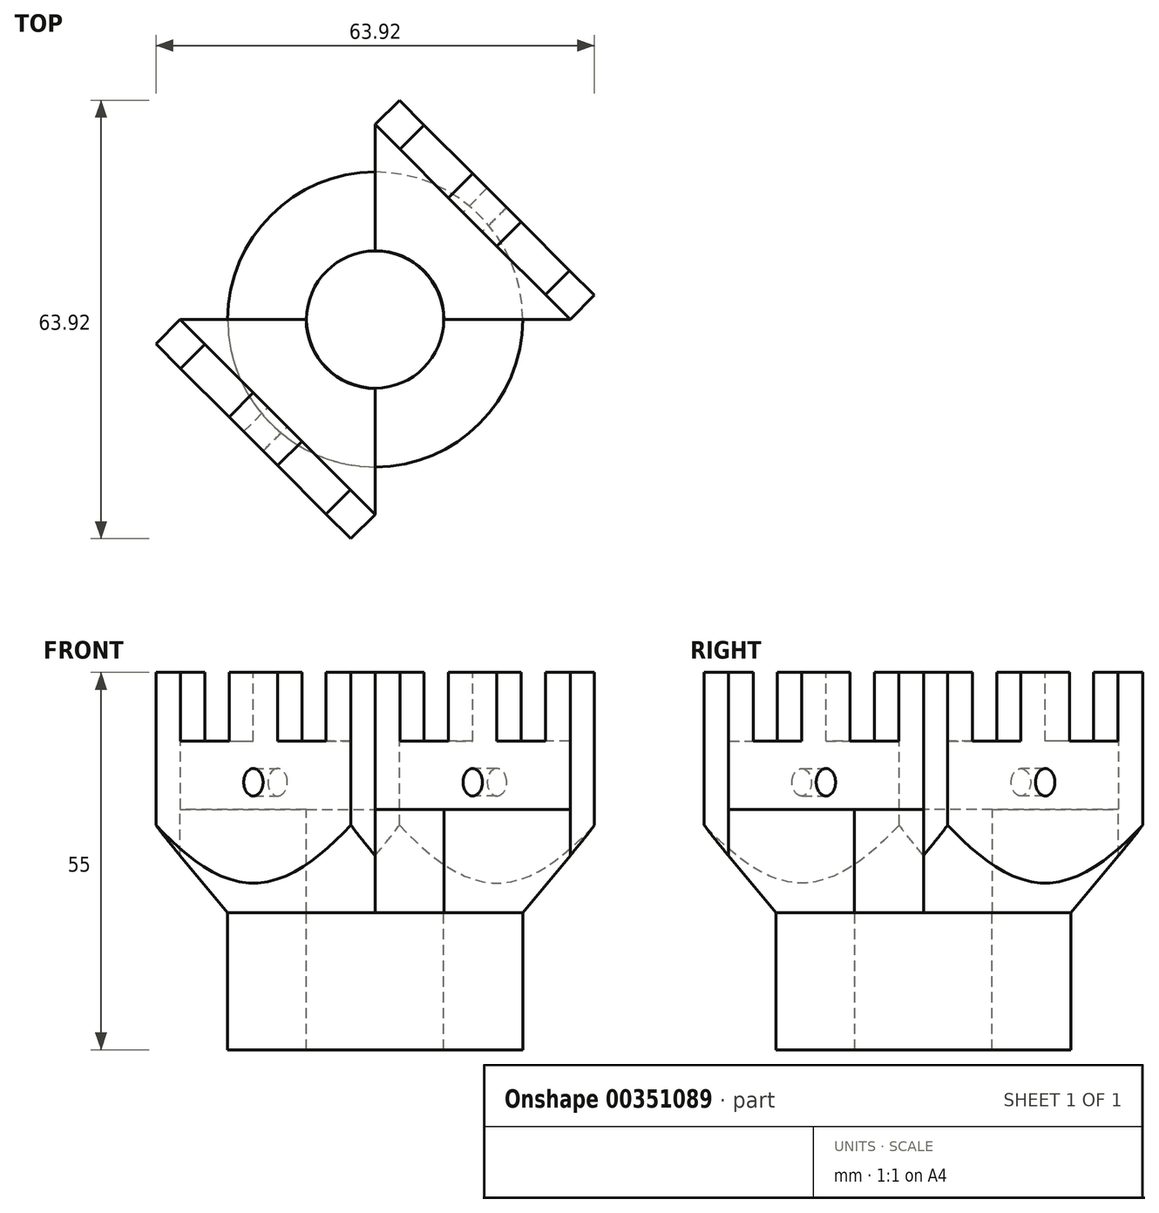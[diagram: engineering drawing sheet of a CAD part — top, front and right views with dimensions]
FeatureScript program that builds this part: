
annotation { "Feature Type Name" : "Feature", "Feature Type Description" : "" }
export const myFeature = defineFeature(function(context is Context, id is Id, definition is map)
    precondition{}
    {
        {
            var Q0;
            Q0=qCreatedBy(makeId("Top.planeOp"),FACE);
            var sketch = newSketch(context, id + "F0", { "sketchPlane" : qUnion([Q0])});
            skCircle(sketch, "E0", {"center": v(0, 0) * mm, "radius": 21.5 * mm});
            skSolve(sketch);
        }
        {
            var Q0;
            Q0=makeQuery(id+"F0.imprint","IMPRINT",FACE,{"disambiguationData":[TD([[makeQuery(id+"F0.imprint","IMPRINT",EDGE,{"derivedFrom":sQuery(id+"F0.wireOp",EDGE,"E0")}),1.0]])]});
            extrude(context, id + "F1", {"entities" : qUnion([Q0]), "depth" : -20 * mm});
        }
        {
            var Q0;
            Q0=makeQuery(id+"F1.opExtrude","CAP_FACE",FACE,{"disambiguationData":[OSD([sQuery(id+"F0.wireOp",EDGE,"E0")])],"isStart":true});
            var sketch = newSketch(context, id + "F2", { "sketchPlane" : qUnion([Q0])});
            skCircle(sketch, "E1", {"center": v(0, 0) * mm, "radius": 10 * mm});
            skSolve(sketch);
        }
        {
            var Q0;
            Q0=makeQuery(id+"F2.imprint","IMPRINT",FACE,{"disambiguationData":[TD([[makeQuery(id+"F2.imprint","IMPRINT",EDGE,{"derivedFrom":sQuery(id+"F2.wireOp",EDGE,"E1")}),1.0]])]});
            extrude(context, id + "F3", {"entities" : qUnion([Q0]), "operationType" : NewBodyOperationType.REMOVE, "endBound" : BoundingType.THROUGH_ALL, "oppositeDirection" : true, "depth" : 25 * mm});
        }
        {
            var Q0;
            Q0=makeQuery(id+"F1.opExtrude","CAP_FACE",FACE,{"disambiguationData":[OSD([sQuery(id+"F0.wireOp",EDGE,"E0")])],"isStart":true});
            var sketch = newSketch(context, id + "F4", { "sketchPlane" : qUnion([Q0])});
            skLineSegment(sketch, "E2.bottom", {"start": v(20.1, 20.1) * mm, "end": v(-20.1, 20.1) * mm, "construction": true});
            skLineSegment(sketch, "E2.top", {"start": v(20.1, -20.1) * mm, "end": v(-20.1, -20.1) * mm, "construction": true});
            skLineSegment(sketch, "E2.left", {"start": v(20.1, 20.1) * mm, "end": v(20.1, -20.1) * mm, "construction": true});
            skLineSegment(sketch, "E2.right", {"start": v(-20.1, 20.1) * mm, "end": v(-20.1, -20.1) * mm, "construction": true});
            skPoint(sketch, "E2.middle", {"position": v(0, 0) * mm});
            skLineSegment(sketch, "E3", {"start": v(0, 0) * mm, "end": v(20.1, 0) * mm, "construction": true});
            skLineSegment(sketch, "E4", {"start": v(20.1, 0) * mm, "end": v(21.5, 0) * mm, "construction": true});
            skSolve(sketch);
        }
        {
            var Q0;
            Q0=qCreatedBy(makeId("Front.planeOp"),FACE);
            var sketch = newSketch(context, id + "F5", { "sketchPlane" : qUnion([Q0])});
            skLineSegment(sketch, "E5", {"start": v(10.05, 0) * mm, "end": v(10.05, 15) * mm});
            skLineSegment(sketch, "E6", {"start": v(10.05, 15) * mm, "end": v(26.57, 15) * mm});
            skLineSegment(sketch, "E7", {"start": v(31.85, 12.37) * mm, "end": v(21.5, 0) * mm});
            skLineSegment(sketch, "E8", {"start": v(21.5, 0) * mm, "end": v(10.05, 0) * mm});
            skPoint(sketch, "E9.visualSharp", {"position": v(34.05, 15) * mm});
            skLineSegment(sketch, "E10", {"start": v(0, 0) * mm, "end": v(0, 17.69) * mm, "construction": true});
            skLineSegment(sketch, "E11", {"start": v(31.85, 12.37) * mm, "end": v(34.05, 15) * mm});
            skLineSegment(sketch, "E12", {"start": v(26.57, 15) * mm, "end": v(34.05, 15) * mm});
            skSolve(sketch);
        }
        {
            var Q0;
            Q0=makeQuery(id+"F5.imprint","IMPRINT",FACE,{"disambiguationData":[TD([[makeQuery(id+"F5.imprint","IMPRINT",EDGE,{"derivedFrom":sQuery(id+"F5.wireOp",EDGE,"E5")}),-1.0]])]});
            var Q1;
            Q1=sQuery(id+"F5.wireOp",EDGE,"E10");
            revolve(context, id + "F6", {"operationType" : NewBodyOperationType.ADD, "entities" : qUnion([Q0]), "axis" : qUnion([Q1]), "revolveType" : RevolveType.ONE_DIRECTION, "angle" : 90 * degree});
        }
        {
            var Q0;
            Q0=makeQuery(id+"F6.opRevolve","SWEPT_FACE",FACE,{"disambiguationData":[OSD([sQuery(id+"F5.wireOp",EDGE,"E6")])]});
            var sketch = newSketch(context, id + "F7", { "sketchPlane" : qUnion([Q0])});
            skLineSegment(sketch, "E13", {"start": v(0, 0) * mm, "end": v(-9.85, -2.02) * mm, "construction": true});
            skLineSegment(sketch, "E14", {"start": v(0, 0) * mm, "end": v(9.85, 2.02) * mm, "construction": true});
            skLineSegment(sketch, "E15.bottom", {"start": v(0, 28.43) * mm, "end": v(-28.43, 0) * mm, "construction": true});
            skLineSegment(sketch, "E15.top", {"start": v(28.43, 0) * mm, "end": v(0, -28.43) * mm, "construction": true});
            skLineSegment(sketch, "E15.left", {"start": v(0, 28.43) * mm, "end": v(28.43, 0) * mm, "construction": true});
            skLineSegment(sketch, "E15.right", {"start": v(-28.43, 0) * mm, "end": v(0, -28.43) * mm, "construction": true});
            skPoint(sketch, "E15.middle", {"position": v(0, 0) * mm});
            skLineSegment(sketch, "E16.bottom", {"start": v(0, 28.43) * mm, "end": v(28.43, 0) * mm});
            skLineSegment(sketch, "E16.top", {"start": v(3.54, 31.96) * mm, "end": v(31.96, 3.54) * mm});
            skLineSegment(sketch, "E16.left", {"start": v(0, 28.43) * mm, "end": v(3.54, 31.96) * mm});
            skLineSegment(sketch, "E16.right", {"start": v(28.43, 0) * mm, "end": v(31.96, 3.54) * mm});
            skSolve(sketch);
        }
        {
            var Q0;
            Q0=makeQuery(id+"F7.imprint","IMPRINT",FACE,{"disambiguationData":[TD([[makeQuery(id+"F7.imprint","IMPRINT",EDGE,{"derivedFrom":sQuery(id+"F7.wireOp",EDGE,"E16.top")}),1.0]])]});
            extrude(context, id + "F8", {"entities" : qUnion([Q0]), "operationType" : NewBodyOperationType.REMOVE, "endBound" : BoundingType.THROUGH_ALL, "oppositeDirection" : true, "depth" : 25 * mm});
        }
        {
            var Q0;
            Q0=makeQuery(id+"F7.imprint","IMPRINT",FACE,{"disambiguationData":[TD([[makeQuery(id+"F7.imprint","IMPRINT",EDGE,{"derivedFrom":sQuery(id+"F7.wireOp",EDGE,"E16.bottom")}),1.0]])]});
            extrude(context, id + "F9", {"entities" : qUnion([Q0]), "operationType" : NewBodyOperationType.ADD, "depth" : 20 * mm});
        }
        {
            var Q0;
            Q0=makeQuery(id+"F9.opExtrude","SWEPT_FACE",FACE,{"disambiguationData":[OSD([sQuery(id+"F7.wireOp",EDGE,"E16.bottom")])]});
            var sketch = newSketch(context, id + "F10", { "sketchPlane" : qUnion([Q0])});
            skLineSegment(sketch, "E17", {"start": v(0, 35) * mm, "end": v(5, 35) * mm, "construction": true});
            skLineSegment(sketch, "E18", {"start": v(0, 35) * mm, "end": v(-5, 35) * mm, "construction": true});
            skLineSegment(sketch, "E19", {"start": v(-5, 35) * mm, "end": v(-15, 35) * mm});
            skLineSegment(sketch, "E20", {"start": v(-15, 35) * mm, "end": v(-15, 25) * mm});
            skLineSegment(sketch, "E21", {"start": v(-15, 25) * mm, "end": v(-5, 25) * mm});
            skLineSegment(sketch, "E22", {"start": v(-5, 25) * mm, "end": v(-5, 35) * mm});
            skLineSegment(sketch, "E23", {"start": v(5, 35) * mm, "end": v(15, 35) * mm});
            skLineSegment(sketch, "E24", {"start": v(15, 35) * mm, "end": v(15, 25) * mm});
            skLineSegment(sketch, "E25", {"start": v(15, 25) * mm, "end": v(5, 25) * mm});
            skLineSegment(sketch, "E26", {"start": v(5, 25) * mm, "end": v(5, 35) * mm});
            skLineSegment(sketch, "E27", {"start": v(0, 15) * mm, "end": v(0, 19) * mm});
            skPoint(sketch, "E27.endSnap0", {"position": v(0, 15) * mm});
            skCircle(sketch, "E28", {"center": v(0, 19) * mm, "radius": 2 * mm});
            skSolve(sketch);
        }
        {
            var Q0;
            Q0=makeQuery(id+"F10.imprint","IMPRINT",FACE,{"disambiguationData":[TD([[makeQuery(id+"F10.imprint","IMPRINT",EDGE,{"derivedFrom":sQuery(id+"F10.wireOp",EDGE,"E19")}),-1.0]])]});
            extrude(context, id + "F11", {"entities" : qUnion([Q0]), "operationType" : NewBodyOperationType.REMOVE, "endBound" : BoundingType.THROUGH_ALL, "oppositeDirection" : true, "depth" : 25 * mm});
        }
        {
            var Q0;
            Q0=makeQuery(id+"F10.imprint","IMPRINT",FACE,{"disambiguationData":[TD([[makeQuery(id+"F10.imprint","IMPRINT",EDGE,{"derivedFrom":sQuery(id+"F10.wireOp",EDGE,"E23")}),-1.0]])]});
            extrude(context, id + "F12", {"entities" : qUnion([Q0]), "operationType" : NewBodyOperationType.REMOVE, "endBound" : BoundingType.THROUGH_ALL, "oppositeDirection" : true, "depth" : 25 * mm});
        }
        {
            var Q0;
            Q0=makeQuery(id+"F10.imprint","IMPRINT",FACE,{"disambiguationData":[TD([[makeQuery(id+"F10.imprint","IMPRINT",EDGE,{"derivedFrom":sQuery(id+"F10.wireOp",EDGE,"E28")}),1.0]])]});
            extrude(context, id + "F13", {"entities" : qUnion([Q0]), "operationType" : NewBodyOperationType.REMOVE, "endBound" : BoundingType.THROUGH_ALL, "oppositeDirection" : true, "depth" : 25 * mm});
        }
        {
            var Q0;
            Q0=makeQuery(id+"F9.opExtrude","SWEPT_FACE",FACE,{"disambiguationData":[OSD([sQuery(id+"F7.wireOp",EDGE,"E16.bottom")])]});
            var Q1;
            Q1=qCreatedBy(makeId("Origin.pointOp"),VERTEX);
            cPlane(context, id + "F14", {"entities" : qUnion([Q0, Q1]), "cplaneType" : CPlaneType.PLANE_POINT, "offset" : 25 * mm, "width" : 150 * mm, "height" : 150 * mm});
        }
        {
            var Q0;
            Q0=makeQuery(id+"F1.opExtrude","SWEPT_BODY",BODY,{"disambiguationData":[OSD([sQuery(id+"F0.wireOp",EDGE,"E0")])]});
            var Q1;
            Q1=qCreatedBy(id+"F14.planeOp",FACE);
            mirror(context, id + "F15", {"operationType" : NewBodyOperationType.ADD, "entities" : qUnion([Q0]), "mirrorPlane" : qUnion([Q1])});
        }
    });
